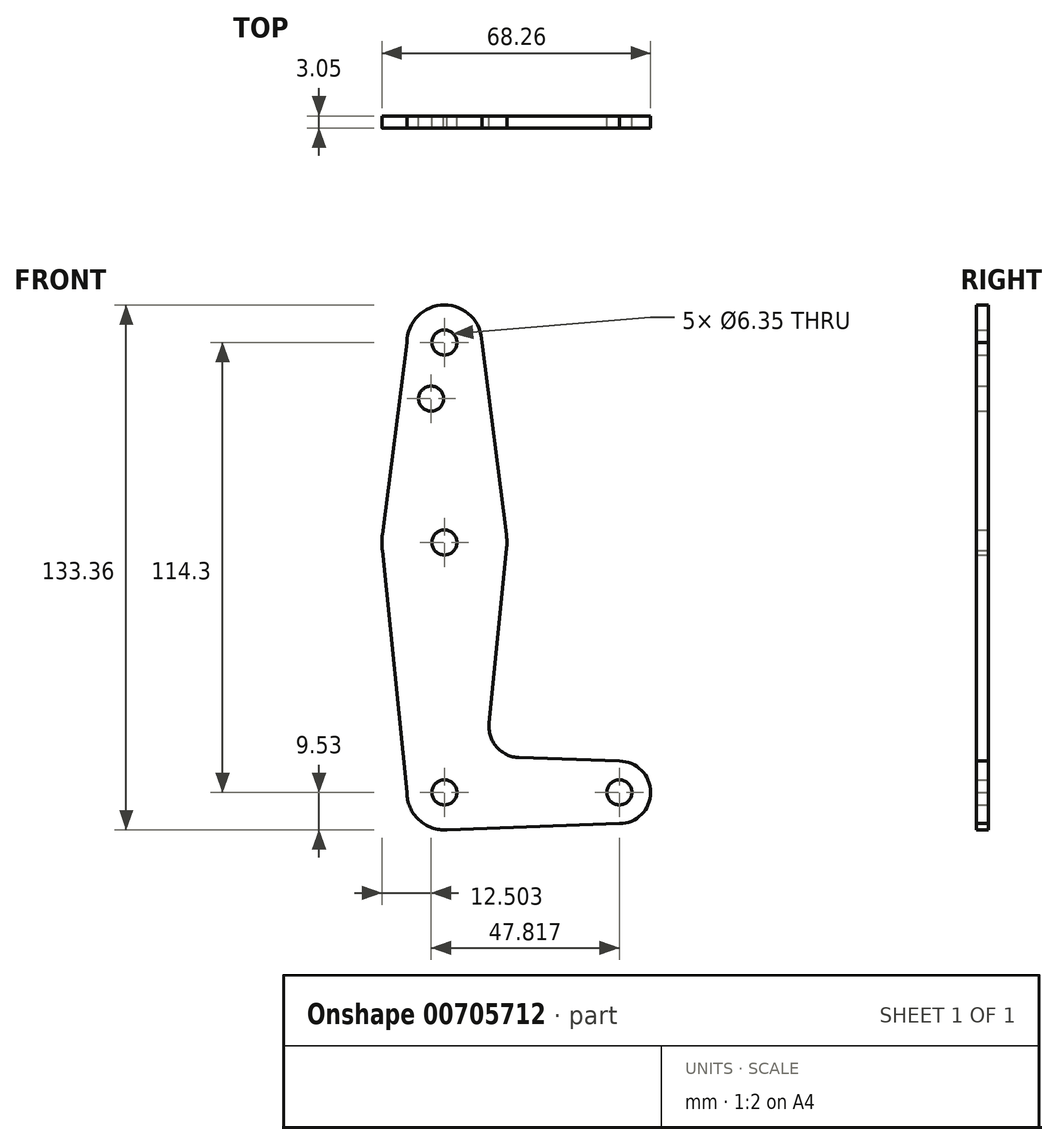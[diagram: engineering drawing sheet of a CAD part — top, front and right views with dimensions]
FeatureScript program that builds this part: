
annotation { "Feature Type Name" : "Feature", "Feature Type Description" : "" }
export const myFeature = defineFeature(function(context is Context, id is Id, definition is map)
    precondition{}
    {
        {
            var Q0;
            Q0=qCreatedBy(makeId("Front.planeOp"),FACE);
            var sketch = newSketch(context, id + "F0", { "sketchPlane" : qUnion([Q0])});
            skLineSegment(sketch, "E0", {"start": v(0, 0) * mm, "end": v(0, 8.74) * mm});
            skLineSegment(sketch, "E1", {"start": v(0, 0) * mm, "end": v(44.45, 0) * mm});
            skCircle(sketch, "E2", {"center": v(0, 114.3) * mm, "radius": 9.53 * mm});
            skArc(sketch, "E3", {"start": v(0.68, 9.5) * mm, "mid": v(-7.79, -5.48) * mm, "end": v(9.17, -2.56) * mm});
            skCircle(sketch, "E4", {"center": v(44.45, 0) * mm, "radius": 7.94 * mm});
            skLineSegment(sketch, "E5", {"start": v(0, 63.5) * mm, "end": v(0, 104.78) * mm});
            skLineSegment(sketch, "E6", {"start": v(0, 114.3) * mm, "end": v(0, 104.78) * mm});
            skLineSegment(sketch, "E7", {"start": v(18.97, 8.85) * mm, "end": v(44.45, 7.94) * mm});
            skLineSegment(sketch, "E8", {"start": v(0, -9.52) * mm, "end": v(44.45, -7.94) * mm});
            skCircle(sketch, "E9", {"center": v(0, 114.3) * mm, "radius": 3.18 * mm});
            skCircle(sketch, "E10", {"center": v(-3.37, 100.03) * mm, "radius": 3.18 * mm});
            skCircle(sketch, "E11", {"center": v(0, 63.5) * mm, "radius": 15.88 * mm});
            skLineSegment(sketch, "E12", {"start": v(-9.53, 114.3) * mm, "end": v(-15.75, 65.5) * mm});
            skLineSegment(sketch, "E13", {"start": v(9.53, 114.3) * mm, "end": v(15.75, 65.5) * mm});
            skCircle(sketch, "E14", {"center": v(0, 63.5) * mm, "radius": 3.18 * mm});
            skCircle(sketch, "E15", {"center": v(0, 0) * mm, "radius": 3.18 * mm});
            skCircle(sketch, "E16", {"center": v(44.45, 0) * mm, "radius": 3.18 * mm});
            skArc(sketch, "E17", {"start": v(-0.58, 9.5) * mm, "mid": v(-0.3, 9.12) * mm, "end": v(0, 8.74) * mm});
            skArc(sketch, "E18.trimOffspring", {"start": v(8.86, 3.5) * mm, "mid": v(9.38, 3.43) * mm, "end": v(9.91, 3.36) * mm});
            skLineSegment(sketch, "E19", {"start": v(-15.75, 61.5) * mm, "end": v(-9.52, 0) * mm});
            skLineSegment(sketch, "E20.trimOffspring", {"start": v(9.57, 0) * mm, "end": v(9.53, -0.48) * mm});
            skLineSegment(sketch, "E21", {"start": v(15.8, 61.91) * mm, "end": v(11.34, 17.59) * mm});
            skCircle(sketch, "E22", {"center": v(0, 0) * mm, "radius": 9.53 * mm});
            skArc(sketch, "E23.filletArc", {"start": v(11.34, 17.59) * mm, "mid": v(13.26, 11.57) * mm, "end": v(18.97, 8.85) * mm});
            skLineSegment(sketch, "E24.trimOffspring", {"start": v(0, 9.52) * mm, "end": v(0, 63.5) * mm});
            skSolve(sketch);
        }
        {
            var Q0;
            Q0 = qSketchRegion(id + "F0", true);
            var Q1;
            {var subQ6=sQuery(id+"F0.wireOp",EDGE,"E22");var subQ8=makeQuery(id+"F0.imprint","IMPRINT",VERTEX,{"disambiguationData":[OD(0.0)],"derivedFrom":subQ6});Q1=makeQuery(id+"F0.imprint","IMPRINT",FACE,{"disambiguationData":[TD([[makeQuery(id+"F0.imprint","IMPRINT",EDGE,{"disambiguationData":[TD([[subQ8,-1.0]])],"derivedFrom":subQ6}),1.0]])]});}
            extrude(context, id + "F1", {"entities" : qUnion([Q0, Q1]), "depth" : 3.05 * mm, "offsetDistance" : 25.4 * mm});
        }
    });
